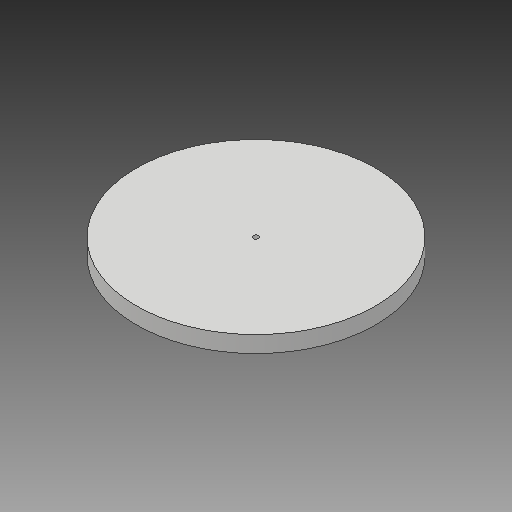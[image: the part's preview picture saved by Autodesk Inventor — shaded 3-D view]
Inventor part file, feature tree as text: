
AUTODESK INVENTOR PART (.ipt)
format: ipt  version: 2017 (Build 210142000, 142)  size: 95,744 bytes
history: native  units: mm
features: sketch x3, extrude x2
ambient origin geometry x8: Origin, YZ Plane, XZ Plane, XY Plane, X Axis, Y Axis, Z Axis, Center Point
bodies: Solid1 (feature_tree)
feature tree (5):
  extrude  "Cuerpo"  Depth=3.0mm TaperAngle=0.0deg
  extrude  "Manivela"  Depth=10.0mm
  sketch  "Sketch1"  dims[d0=43.6mm d1=3.0mm d2=0.0mm]
  sketch  "Sketch2"  dims[d4=14.3mm d5=10.0mm]
  sketch  "Sketch3"  dims[d6=3.0mm d7=0.0mm d8=1.0mm d9=6.0mm d10=4.0mm d11=2.0mm d12=90.0deg d13=8.0mm d14=20.594885mm]
